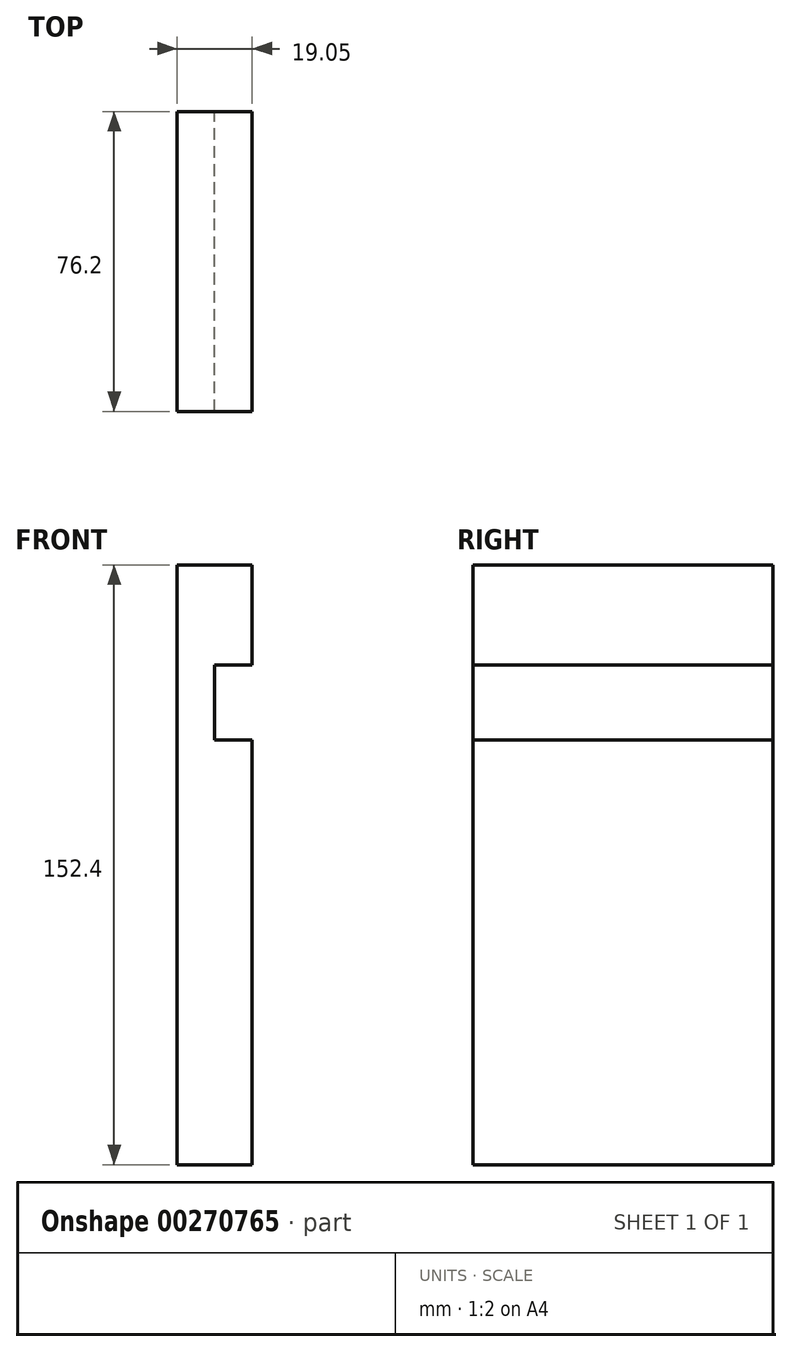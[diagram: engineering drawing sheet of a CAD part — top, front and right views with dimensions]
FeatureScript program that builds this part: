
annotation { "Feature Type Name" : "Feature", "Feature Type Description" : "" }
export const myFeature = defineFeature(function(context is Context, id is Id, definition is map)
    precondition{}
    {
        {
            var Q0;
            Q0=qCreatedBy(makeId("Front.planeOp"),FACE);
            var sketch = newSketch(context, id + "F0", { "sketchPlane" : qUnion([Q0])});
            skLineSegment(sketch, "E0", {"start": v(-76, 76) * mm, "end": v(-56.95, 76) * mm});
            skLineSegment(sketch, "E1", {"start": v(-56.95, 76) * mm, "end": v(-56.95, 50.6) * mm});
            skLineSegment(sketch, "E2", {"start": v(-56.95, 50.6) * mm, "end": v(-66.47, 50.6) * mm});
            skLineSegment(sketch, "E3", {"start": v(-66.47, 50.6) * mm, "end": v(-66.47, 31.55) * mm});
            skLineSegment(sketch, "E4", {"start": v(-66.47, 31.55) * mm, "end": v(-56.95, 31.55) * mm});
            skLineSegment(sketch, "E5", {"start": v(-56.95, 31.55) * mm, "end": v(-56.95, -76.4) * mm});
            skLineSegment(sketch, "E6", {"start": v(-56.95, -76.4) * mm, "end": v(-76, -76.4) * mm});
            skLineSegment(sketch, "E7", {"start": v(-76, -76.4) * mm, "end": v(-76, 76) * mm});
            skSolve(sketch);
        }
        {
            var Q0;
            Q0=makeQuery(id+"F0.imprint","IMPRINT",FACE,{"disambiguationData":[TD([[makeQuery(id+"F0.imprint","IMPRINT",EDGE,{"derivedFrom":sQuery(id+"F0.wireOp",EDGE,"E0")}),-1.0]])]});
            extrude(context, id + "F1", {"entities" : qUnion([Q0]), "depth" : 76.2 * mm});
        }
    });
